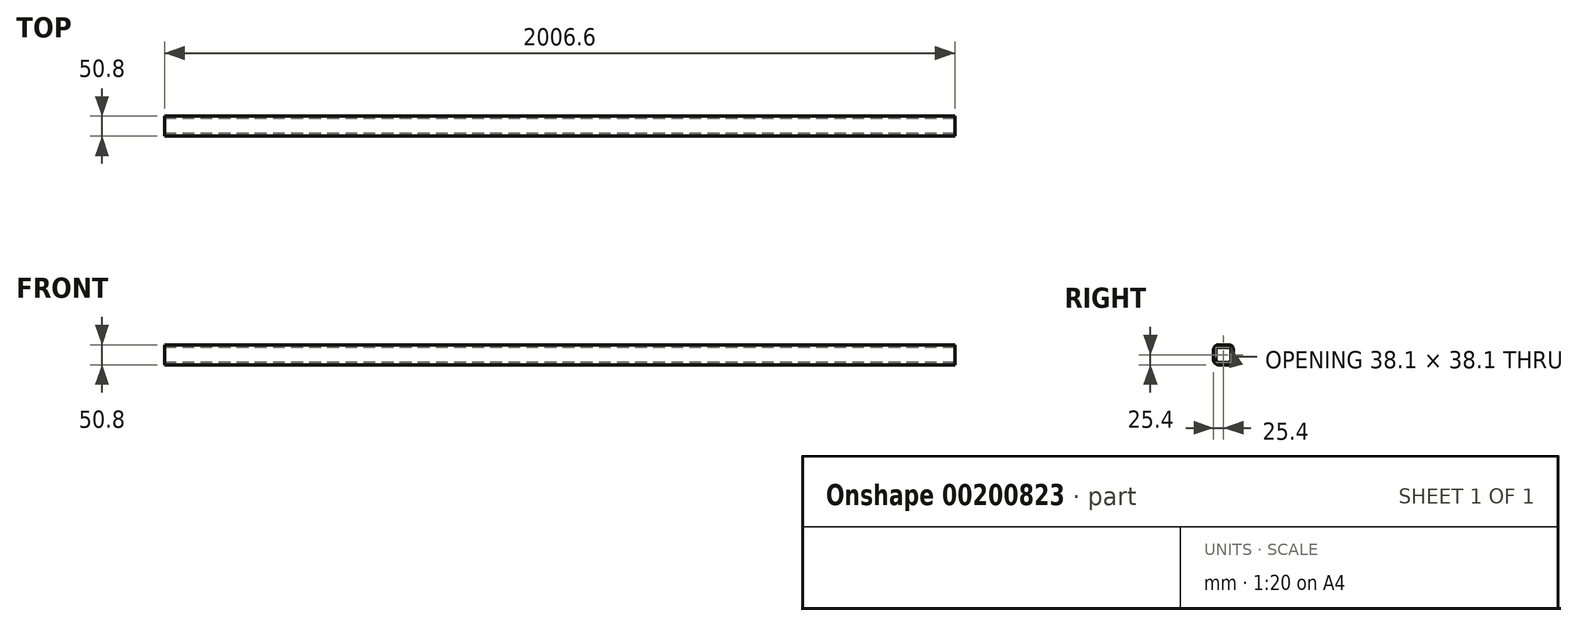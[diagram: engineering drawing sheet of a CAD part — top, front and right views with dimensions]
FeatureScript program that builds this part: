
annotation { "Feature Type Name" : "Feature", "Feature Type Description" : "" }
export const myFeature = defineFeature(function(context is Context, id is Id, definition is map)
    precondition{}
    {
        {
            var Q0;
            Q0=qCreatedBy(makeId("Right.planeOp"),FACE);
            var sketch = newSketch(context, id + "F0", { "sketchPlane" : qUnion([Q0])});
            skLineSegment(sketch, "E0.bottom", {"start": v(12.7, 25.4) * mm, "end": v(-12.7, 25.4) * mm});
            skLineSegment(sketch, "E0.top", {"start": v(12.7, -25.4) * mm, "end": v(-12.7, -25.4) * mm});
            skLineSegment(sketch, "E0.left", {"start": v(25.4, 12.7) * mm, "end": v(25.4, -12.7) * mm});
            skLineSegment(sketch, "E0.right", {"start": v(-25.4, 12.7) * mm, "end": v(-25.4, -12.7) * mm});
            skPoint(sketch, "E0.middle", {"position": v(0, 0) * mm});
            skLineSegment(sketch, "E1.bottom", {"start": v(12.7, 19.05) * mm, "end": v(-12.7, 19.05) * mm});
            skLineSegment(sketch, "E1.top", {"start": v(12.7, -19.05) * mm, "end": v(-12.7, -19.05) * mm});
            skLineSegment(sketch, "E1.left", {"start": v(19.05, 12.7) * mm, "end": v(19.05, -12.7) * mm});
            skLineSegment(sketch, "E1.right", {"start": v(-19.05, 12.7) * mm, "end": v(-19.05, -12.7) * mm});
            skPoint(sketch, "E2.visualSharp", {"position": v(-25.4, 25.4) * mm});
            skArc(sketch, "E2.filletArc", {"start": v(-12.7, 25.4) * mm, "mid": v(-21.68, 21.68) * mm, "end": v(-25.4, 12.7) * mm});
            skPoint(sketch, "E3.visualSharp", {"position": v(-25.4, -25.4) * mm});
            skArc(sketch, "E3.filletArc", {"start": v(-25.4, -12.7) * mm, "mid": v(-21.68, -21.68) * mm, "end": v(-12.7, -25.4) * mm});
            skPoint(sketch, "E4.visualSharp", {"position": v(25.4, -25.4) * mm});
            skArc(sketch, "E4.filletArc", {"start": v(12.7, -25.4) * mm, "mid": v(21.68, -21.68) * mm, "end": v(25.4, -12.7) * mm});
            skPoint(sketch, "E5.visualSharp", {"position": v(25.4, 25.4) * mm});
            skArc(sketch, "E5.filletArc", {"start": v(25.4, 12.7) * mm, "mid": v(21.68, 21.68) * mm, "end": v(12.7, 25.4) * mm});
            skPoint(sketch, "E6.visualSharp", {"position": v(19.05, 19.05) * mm});
            skArc(sketch, "E6.filletArc", {"start": v(19.05, 12.7) * mm, "mid": v(17.2, 17.2) * mm, "end": v(12.7, 19.05) * mm});
            skPoint(sketch, "E7.visualSharp", {"position": v(19.05, -19.05) * mm});
            skArc(sketch, "E7.filletArc", {"start": v(12.7, -19.05) * mm, "mid": v(17.2, -17.2) * mm, "end": v(19.05, -12.7) * mm});
            skPoint(sketch, "E8.visualSharp", {"position": v(-19.05, -19.05) * mm});
            skArc(sketch, "E8.filletArc", {"start": v(-19.05, -12.7) * mm, "mid": v(-17.2, -17.2) * mm, "end": v(-12.7, -19.05) * mm});
            skPoint(sketch, "E9.visualSharp", {"position": v(-19.05, 19.05) * mm});
            skArc(sketch, "E9.filletArc", {"start": v(-12.7, 19.05) * mm, "mid": v(-17.2, 17.2) * mm, "end": v(-19.05, 12.7) * mm});
            skSolve(sketch);
        }
        {
            var Q0;
            Q0=makeQuery(id+"F0.imprint","IMPRINT",FACE,{"disambiguationData":[TD([[makeQuery(id+"F0.imprint","IMPRINT",EDGE,{"derivedFrom":sQuery(id+"F0.wireOp",EDGE,"E0.bottom")}),1.0]])]});
            extrude(context, id + "F1", {"entities" : qUnion([Q0]), "depth" : 2006.6 * mm});
        }
    });
